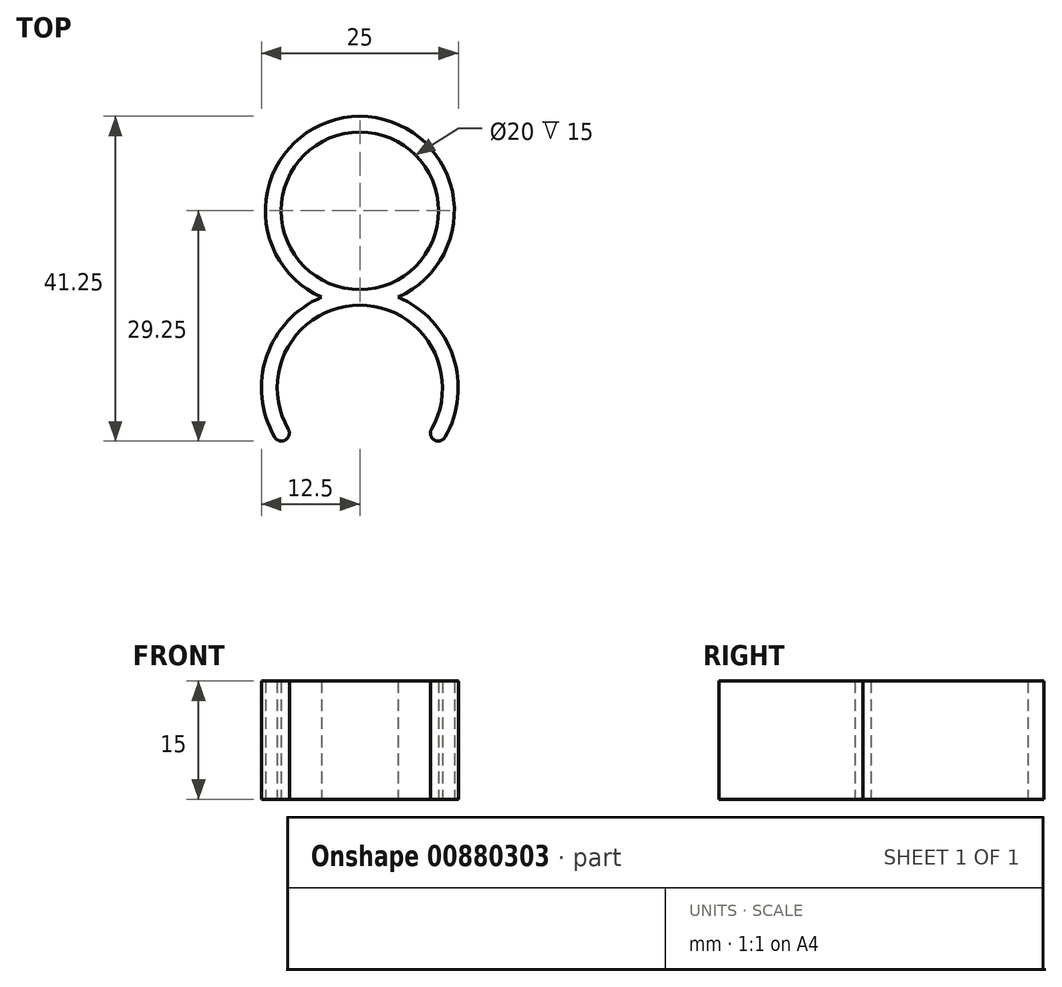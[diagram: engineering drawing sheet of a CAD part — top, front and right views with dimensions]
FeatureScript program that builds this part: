
annotation { "Feature Type Name" : "Feature", "Feature Type Description" : "" }
export const myFeature = defineFeature(function(context is Context, id is Id, definition is map)
    precondition{}
    {
        {
            var Q0;
            Q0=qCreatedBy(makeId("Top.planeOp"),FACE);
            var sketch = newSketch(context, id + "F0", { "sketchPlane" : qUnion([Q0])});
            skCircle(sketch, "E0", {"center": v(0, 0) * mm, "radius": 10 * mm});
            skCircle(sketch, "E1", {"center": v(0, 0) * mm, "radius": 12 * mm});
            skCircle(sketch, "E2", {"center": v(0, -22.5) * mm, "radius": 10.5 * mm});
            skCircle(sketch, "E3", {"center": v(0, -22.5) * mm, "radius": 12.5 * mm});
            skLineSegment(sketch, "E4", {"start": v(0, -22.5) * mm, "end": v(-10.24, -29.67) * mm});
            skLineSegment(sketch, "E5", {"start": v(0, -22.5) * mm, "end": v(10.24, -29.67) * mm});
            skPoint(sketch, "E6", {"position": v(-8.6, -28.52) * mm});
            skPoint(sketch, "E7", {"position": v(8.6, -28.52) * mm});
            skSolve(sketch);
        }
        {
            var Q0;
            {var subQ0=sQuery(id+"F0.wireOp",EDGE,"E0");Q0=makeQuery(id+"F0.imprint","IMPRINT",FACE,{"disambiguationData":[TD([[makeQuery(id+"F0.imprint","IMPRINT",EDGE,{"derivedFrom":subQ0}),-1.0]])]});}
            var Q1;
            {var subQ0=sQuery(id+"F0.wireOp",EDGE,"E3");var subQ1=sQuery(id+"F0.wireOp",EDGE,"E1");var subQ2=makeQuery(id+"F0.imprint","INTERSECT",VERTEX,{"disambiguationData":[OD(0.0)],"derivedFrom":[subQ1,subQ0]});Q1=makeQuery(id+"F0.imprint","IMPRINT",FACE,{"disambiguationData":[TD([[makeQuery(id+"F0.imprint","IMPRINT",EDGE,{"disambiguationData":[TD([[subQ2,-1.0]])],"derivedFrom":subQ1}),1.0]])]});}
            var Q2;
            {var subQ0=sQuery(id+"F0.wireOp",EDGE,"E3");var subQ1=sQuery(id+"F0.wireOp",EDGE,"E1");var subQ2=makeQuery(id+"F0.imprint","INTERSECT",VERTEX,{"disambiguationData":[OD(1.0)],"derivedFrom":[subQ1,subQ0]});Q2=makeQuery(id+"F0.imprint","IMPRINT",FACE,{"disambiguationData":[TD([[makeQuery(id+"F0.imprint","IMPRINT",EDGE,{"disambiguationData":[TD([[subQ2,1.0]])],"derivedFrom":subQ1}),-1.0]])]});}
            var Q3;
            {var subQ0=sQuery(id+"F0.wireOp",EDGE,"E3");var subQ1=sQuery(id+"F0.wireOp",EDGE,"E1");var subQ2=makeQuery(id+"F0.imprint","INTERSECT",VERTEX,{"disambiguationData":[OD(0.0)],"derivedFrom":[subQ1,subQ0]});Q3=makeQuery(id+"F0.imprint","IMPRINT",FACE,{"disambiguationData":[TD([[makeQuery(id+"F0.imprint","IMPRINT",EDGE,{"disambiguationData":[TD([[subQ2,-1.0]])],"derivedFrom":subQ1}),-1.0]])]});}
            extrude(context, id + "F1", {"entities" : qUnion([Q0, Q1, Q2, Q3]), "depth" : 15 * mm, "offsetDistance" : 25 * mm});
        }
        {
            var Q0;
            Q0=makeQuery(id+"F1.opExtrude","SWEPT_EDGE",EDGE,{"disambiguationData":[OSD([sQuery(id+"F0.wireOp",EDGE,"E2"),sQuery(id+"F0.wireOp",EDGE,"E4")])]});
            var Q1;
            Q1=makeQuery(id+"F1.opExtrude","SWEPT_EDGE",EDGE,{"disambiguationData":[OSD([sQuery(id+"F0.wireOp",EDGE,"E3"),sQuery(id+"F0.wireOp",EDGE,"E4")])]});
            var Q2;
            Q2=makeQuery(id+"F1.opExtrude","SWEPT_EDGE",EDGE,{"disambiguationData":[OSD([sQuery(id+"F0.wireOp",EDGE,"E2"),sQuery(id+"F0.wireOp",EDGE,"E5")])]});
            var Q3;
            Q3=makeQuery(id+"F1.opExtrude","SWEPT_EDGE",EDGE,{"disambiguationData":[OSD([sQuery(id+"F0.wireOp",EDGE,"E3"),sQuery(id+"F0.wireOp",EDGE,"E5")])]});
            fillet(context, id + "F2", {"entities" : qUnion([Q0, Q1, Q2, Q3]), "radius" : 1 * mm, "tangentPropagation" : true, "allowEdgeOverflow" : false});
        }
    });
